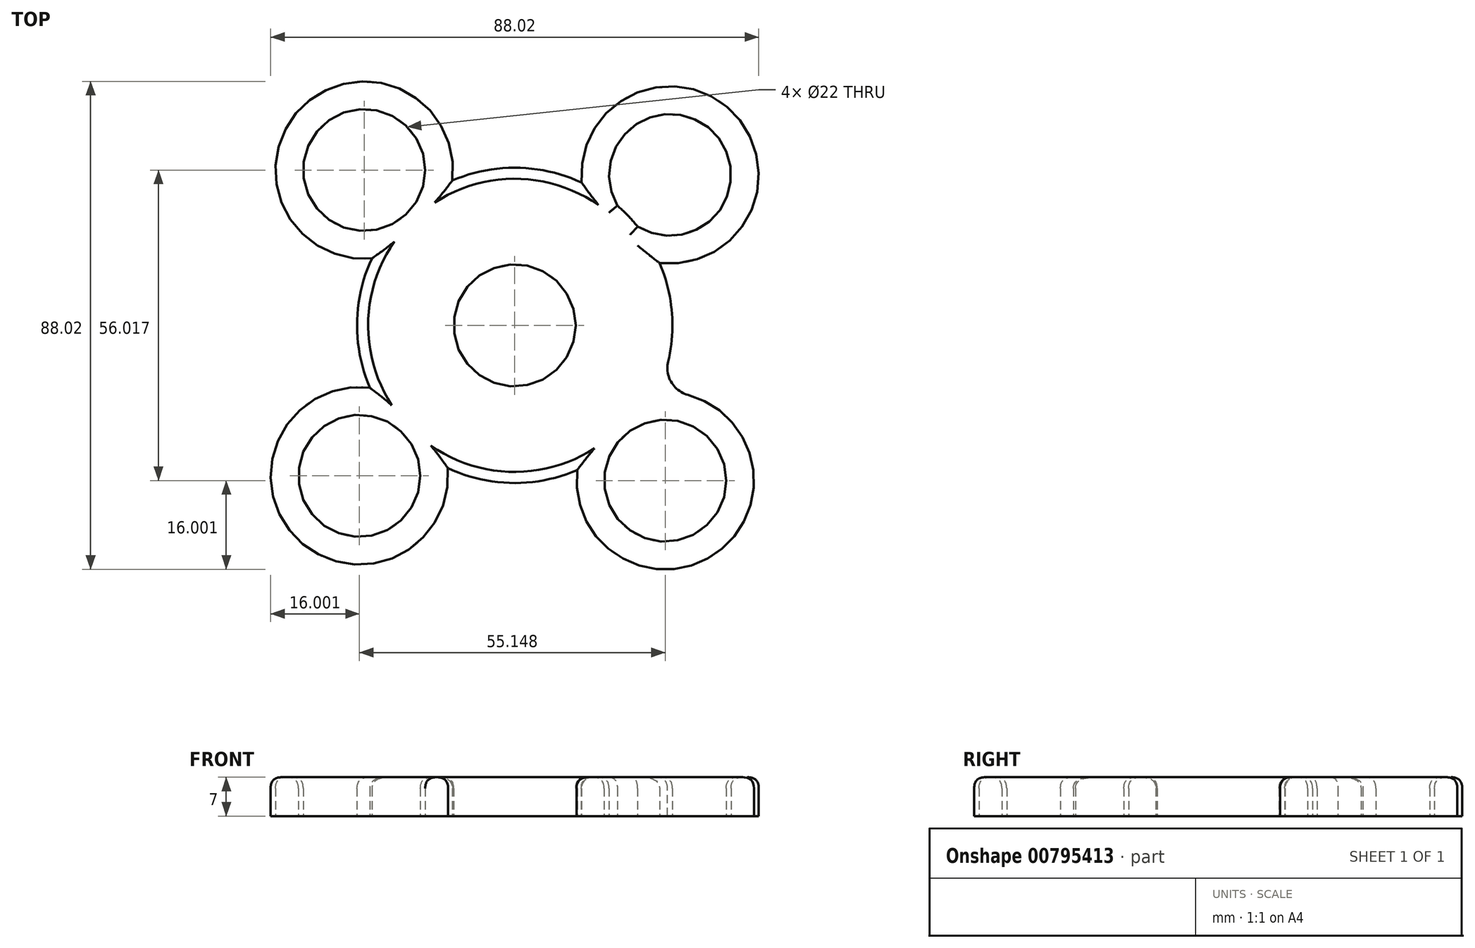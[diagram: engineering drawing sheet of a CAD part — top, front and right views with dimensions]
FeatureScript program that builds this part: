
annotation { "Feature Type Name" : "Feature", "Feature Type Description" : "" }
export const myFeature = defineFeature(function(context is Context, id is Id, definition is map)
    precondition{}
    {
        {
            var Q0;
            Q0=qCreatedBy(makeId("Top.planeOp"),FACE);
            var sketch = newSketch(context, id + "F0", { "sketchPlane" : qUnion([Q0])});
            skCircle(sketch, "E0", {"center": v(0, 0) * mm, "radius": 11 * mm});
            skArc(sketch, "E1", {"start": v(22.16, 17.82) * mm, "mid": v(35.9, 34.8) * mm, "end": v(18.51, 21.59) * mm});
            skCircle(sketch, "E2.1.0", {"center": v(-27.14, 28) * mm, "radius": 11 * mm});
            skCircle(sketch, "E2.2.0", {"center": v(-28, -27.14) * mm, "radius": 11 * mm});
            skCircle(sketch, "E2.3.0", {"center": v(27.14, -28) * mm, "radius": 11 * mm});
            skArc(sketch, "E3.0", {"start": v(-11.25, 26.12) * mm, "mid": v(-38.27, 39.5) * mm, "end": v(-25.75, 12.07) * mm});
            skArc(sketch, "E4.0", {"start": v(-26.12, -11.25) * mm, "mid": v(-39.5, -38.27) * mm, "end": v(-12.07, -25.75) * mm});
            skArc(sketch, "E5.0", {"start": v(26.12, 11.25) * mm, "mid": v(39.5, 38.27) * mm, "end": v(12.07, 25.75) * mm});
            skArc(sketch, "E6.0", {"start": v(11.25, -26.12) * mm, "mid": v(38.27, -39.5) * mm, "end": v(25.75, -12.07) * mm});
            skArc(sketch, "E7", {"start": v(-25.75, 12.07) * mm, "mid": v(-28.43, 0.45) * mm, "end": v(-26.12, -11.25) * mm});
            skArc(sketch, "E8.trimOffspring", {"start": v(-12.07, -25.75) * mm, "mid": v(-0.45, -28.43) * mm, "end": v(11.25, -26.12) * mm});
            skArc(sketch, "E9.trimOffspring", {"start": v(25.75, -12.07) * mm, "mid": v(28.43, -0.45) * mm, "end": v(26.12, 11.25) * mm});
            skArc(sketch, "E10.trimOffspring", {"start": v(22.16, 17.82) * mm, "mid": v(20.42, 19.79) * mm, "end": v(18.51, 21.59) * mm});
            skArc(sketch, "E11.trimOffspring", {"start": v(12.07, 25.75) * mm, "mid": v(0.45, 28.43) * mm, "end": v(-11.25, 26.12) * mm});
            skSolve(sketch);
        }
        {
            var Q0;
            Q0=makeQuery(id+"F0.imprint","IMPRINT",FACE,{"disambiguationData":[TD([[makeQuery(id+"F0.imprint","IMPRINT",EDGE,{"derivedFrom":sQuery(id+"F0.wireOp",EDGE,"E0")}),-1.0]])]});
            extrude(context, id + "F1", {"entities" : qUnion([Q0]), "depth" : 7 * mm, "offsetDistance" : 25 * mm});
        }
        {
            var Q0;
            Q0=makeQuery(id+"F1.opExtrude","SWEPT_EDGE",EDGE,{"disambiguationData":[OSD([sQuery(id+"F0.wireOp",EDGE,"E6.0"),sQuery(id+"F0.wireOp",EDGE,"E9.trimOffspring")])]});
            fillet(context, id + "F2", {"entities" : qUnion([Q0]), "radius" : 5 * mm, "tangentPropagation" : true, "allowEdgeOverflow" : false});
        }
        {
            var Q0;
            Q0=makeQuery(id+"F1.opExtrude","CAP_FACE",FACE,{"disambiguationData":[OSD([sQuery(id+"F0.wireOp",EDGE,"E0"),sQuery(id+"F0.wireOp",EDGE,"E1"),sQuery(id+"F0.wireOp",EDGE,"E2.1.0"),sQuery(id+"F0.wireOp",EDGE,"E2.2.0"),sQuery(id+"F0.wireOp",EDGE,"E2.3.0"),sQuery(id+"F0.wireOp",EDGE,"E3.0"),sQuery(id+"F0.wireOp",EDGE,"E4.0"),sQuery(id+"F0.wireOp",EDGE,"E5.0"),sQuery(id+"F0.wireOp",EDGE,"E6.0"),sQuery(id+"F0.wireOp",EDGE,"E7"),sQuery(id+"F0.wireOp",EDGE,"E8.trimOffspring"),sQuery(id+"F0.wireOp",EDGE,"E9.trimOffspring"),sQuery(id+"F0.wireOp",EDGE,"E10.trimOffspring"),sQuery(id+"F0.wireOp",EDGE,"E11.trimOffspring")])],"isStart":false});
            fillet(context, id + "F3", {"entities" : qUnion([Q0]), "radius" : 2 * mm, "rho" : 0.5, "crossSection" : FilletCrossSection.CONIC, "allowEdgeOverflow" : false});
        }
    });
